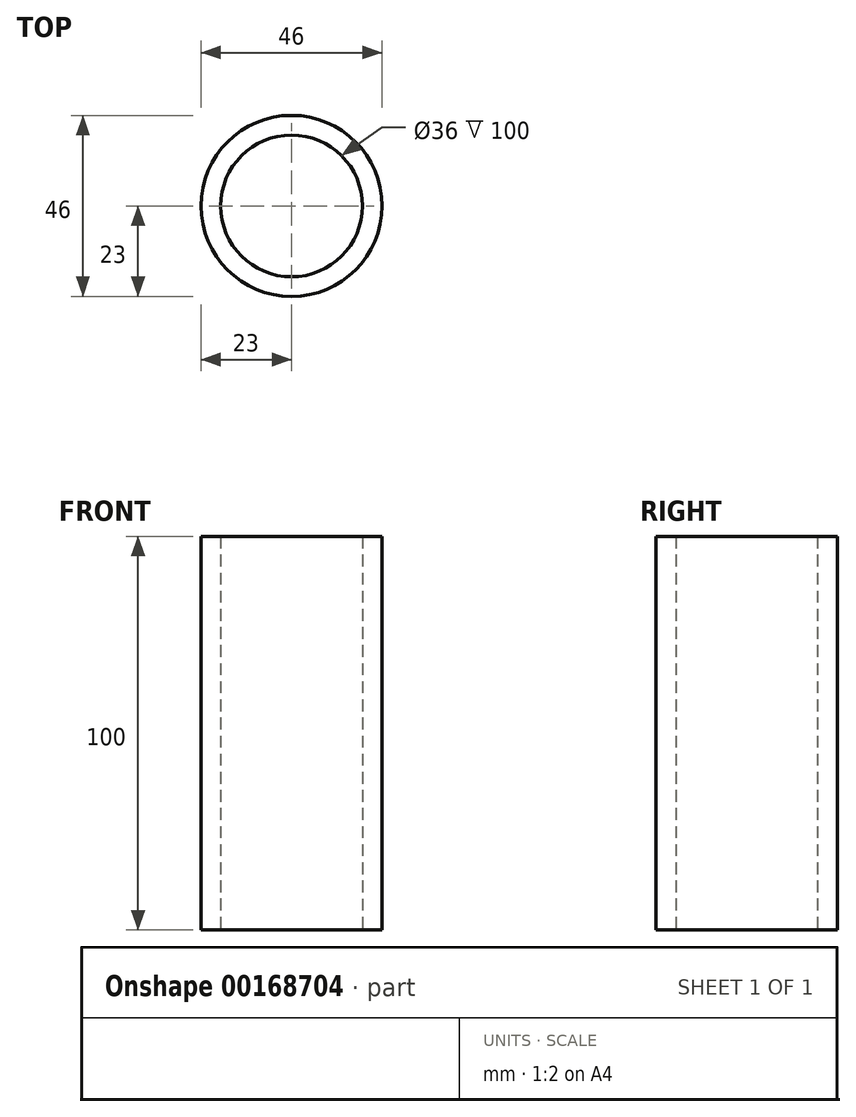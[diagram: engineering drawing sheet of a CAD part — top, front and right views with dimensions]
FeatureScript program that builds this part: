
annotation { "Feature Type Name" : "Feature", "Feature Type Description" : "" }
export const myFeature = defineFeature(function(context is Context, id is Id, definition is map)
    precondition{}
    {
        {
            var Q0;
            Q0=qCreatedBy(makeId("Top.planeOp"),FACE);
            var sketch = newSketch(context, id + "F0", { "sketchPlane" : qUnion([Q0])});
            skCircle(sketch, "E0", {"center": v(0, 0) * mm, "radius": 23 * mm});
            skCircle(sketch, "E1", {"center": v(0, 0) * mm, "radius": 18 * mm});
            skSolve(sketch);
        }
        {
            var Q0;
            Q0=makeQuery(id+"F0.imprint","IMPRINT",FACE,{"disambiguationData":[TD([[makeQuery(id+"F0.imprint","IMPRINT",EDGE,{"derivedFrom":sQuery(id+"F0.wireOp",EDGE,"E0")}),1.0]])]});
            extrude(context, id + "F1", {"entities" : qUnion([Q0]), "endBound" : BoundingType.SYMMETRIC, "depth" : 100 * mm});
        }
    });
